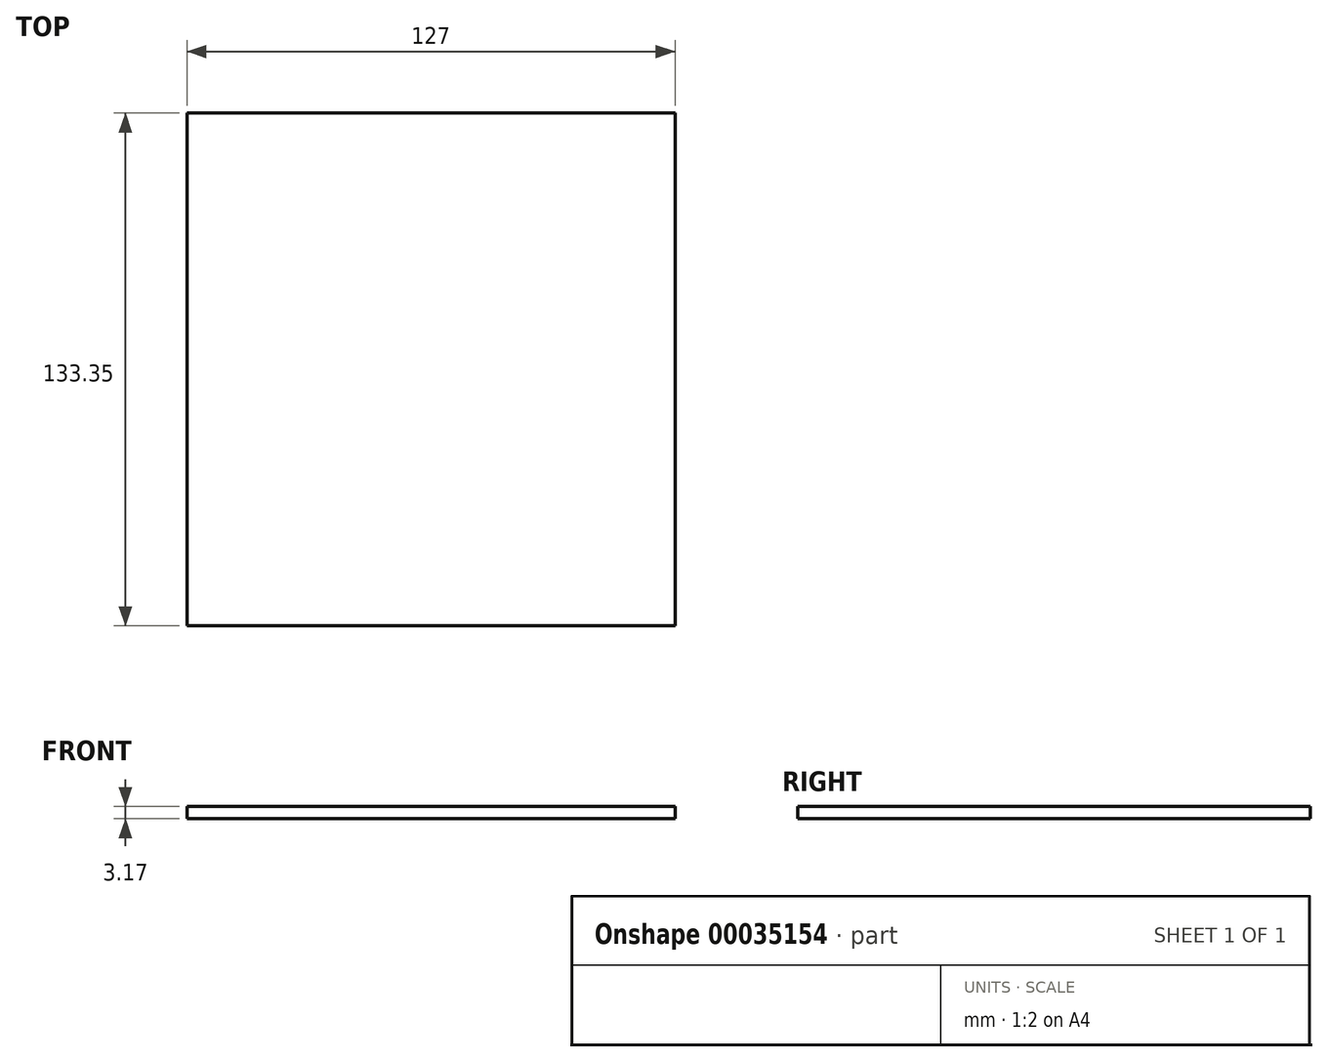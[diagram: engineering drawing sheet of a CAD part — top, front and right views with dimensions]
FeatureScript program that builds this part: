
annotation { "Feature Type Name" : "Feature", "Feature Type Description" : "" }
export const myFeature = defineFeature(function(context is Context, id is Id, definition is map)
    precondition{}
    {
        {
            var Q0;
            Q0=qCreatedBy(makeId("Top.planeOp"),FACE);
            var sketch = newSketch(context, id + "F0", { "sketchPlane" : qUnion([Q0])});
            skLineSegment(sketch, "E0.rect.bottom", {"start": v(56.76, 73.73) * mm, "end": v(-70.24, 73.73) * mm});
            skLineSegment(sketch, "E0.rect.top", {"start": v(56.76, -59.62) * mm, "end": v(-70.24, -59.62) * mm});
            skLineSegment(sketch, "E0.rect.left", {"start": v(56.76, 73.73) * mm, "end": v(56.76, -59.62) * mm});
            skLineSegment(sketch, "E0.rect.right", {"start": v(-70.24, 73.73) * mm, "end": v(-70.24, -59.62) * mm});
            skPoint(sketch, "E0.rect.middle", {"position": v(-6.74, 7.05) * mm});
            skSolve(sketch);
        }
        {
            var Q0;
            Q0=makeQuery(id+"F0.imprint","IMPRINT",FACE,{"disambiguationData":[TD([[makeQuery(id+"F0.imprint","IMPRINT",EDGE,{"derivedFrom":sQuery(id+"F0.wireOp",EDGE,"E0.rect.bottom")}),1.0]])]});
            extrude(context, id + "F1", {"entities" : qUnion([Q0]), "depth" : 3.17 * mm});
        }
    });
